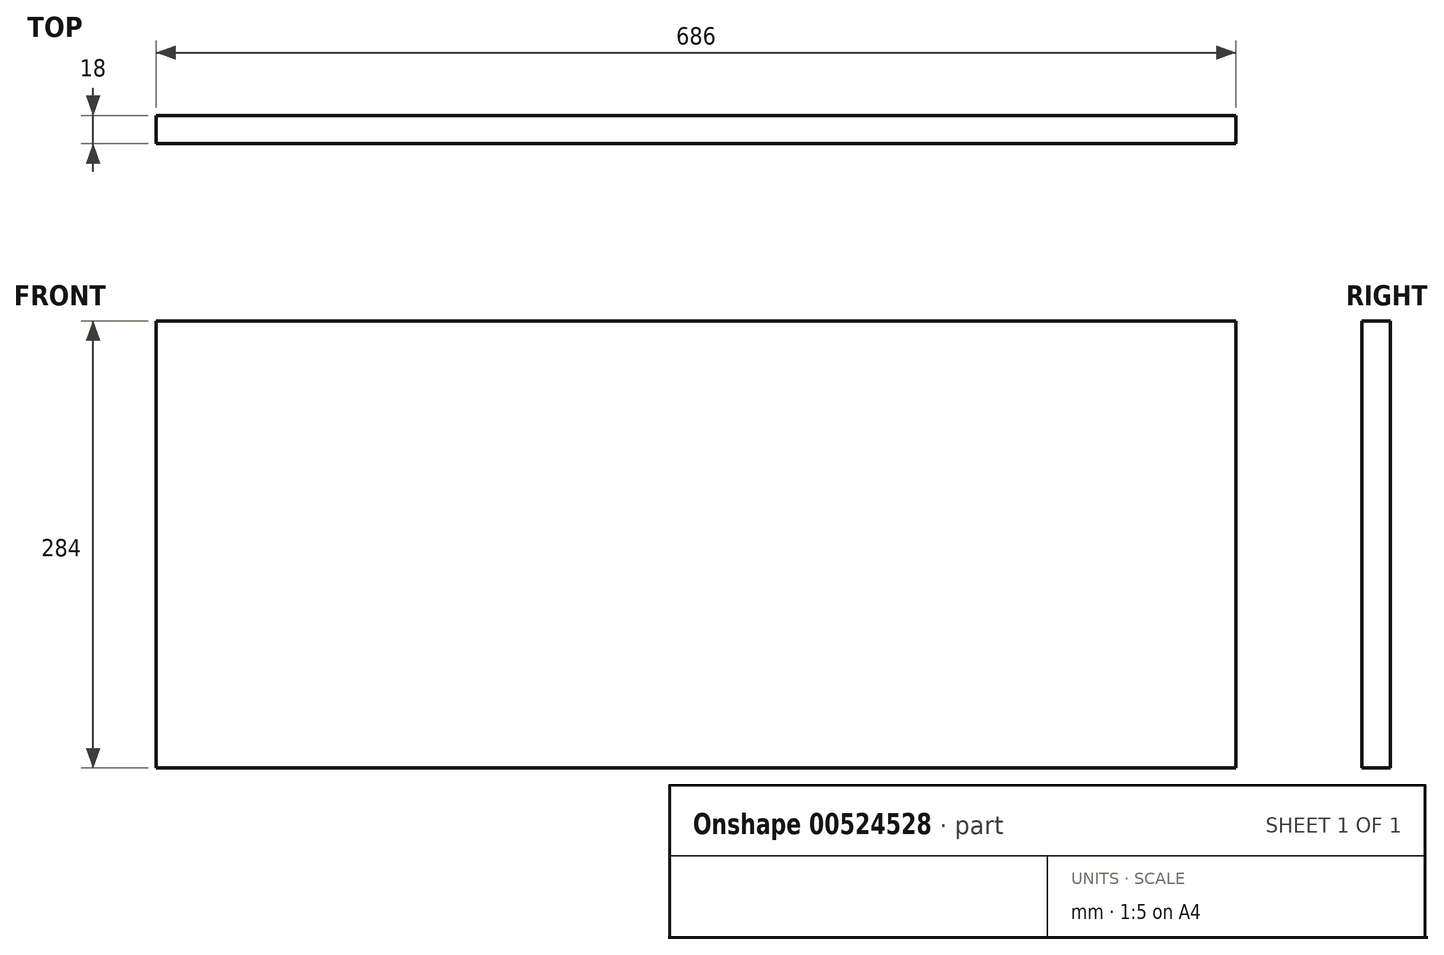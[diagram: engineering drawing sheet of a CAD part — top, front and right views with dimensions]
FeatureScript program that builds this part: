
annotation { "Feature Type Name" : "Feature", "Feature Type Description" : "" }
export const myFeature = defineFeature(function(context is Context, id is Id, definition is map)
    precondition{}
    {
        {
            var Q0;
            Q0=qCreatedBy(makeId("Front.planeOp"),FACE);
            var sketch = newSketch(context, id + "F0", { "sketchPlane" : qUnion([Q0])});
            skLineSegment(sketch, "E0.bottom", {"start": v(0, 0) * mm, "end": v(686, 0) * mm});
            skLineSegment(sketch, "E0.top", {"start": v(0, 284) * mm, "end": v(686, 284) * mm});
            skLineSegment(sketch, "E0.left", {"start": v(0, 0) * mm, "end": v(0, 284) * mm});
            skLineSegment(sketch, "E0.right", {"start": v(686, 0) * mm, "end": v(686, 284) * mm});
            skSolve(sketch);
        }
        {
            var Q0;
            Q0 = qSketchRegion(id + "F0", true);
            extrude(context, id + "F1", {"entities" : qUnion([Q0]), "depth" : 18 * mm, "offsetDistance" : 25 * mm});
        }
    });
